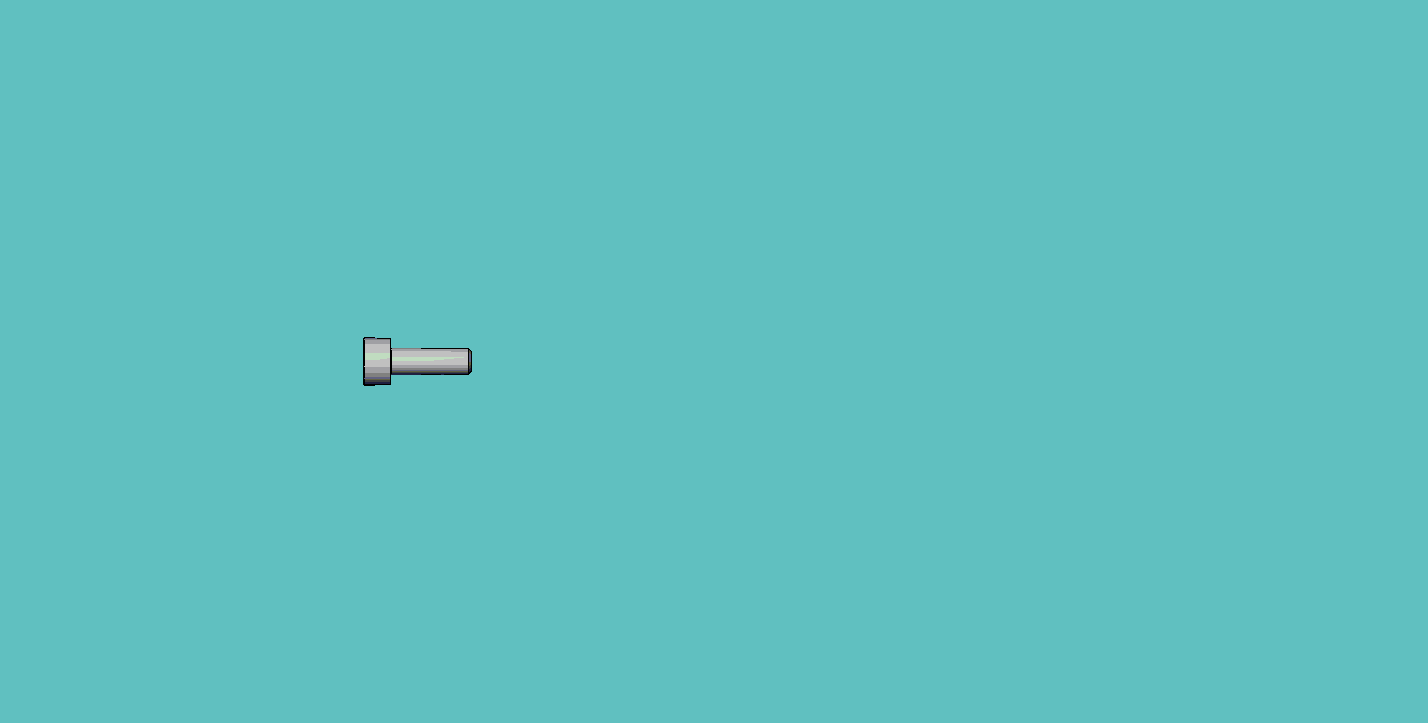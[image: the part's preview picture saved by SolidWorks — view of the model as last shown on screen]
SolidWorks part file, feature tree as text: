
SOLIDWORKS PART (.sldprt)
format: sldprt  version: not decoded by parser v0  size: 192,512 bytes
history: native  units: mm
features: sketch x4, plane x3, fillet x2, cut_revolve x2, material x1, revolve x1, thread x1, cut_extrude x1, pattern_linear x1 (+10 scaffold rows collapsed; 1 parser-record rows omitted)
feature tree (27):
  scaffold x10  (default folders/planes/origin — collapsed)
  material  "Material <not specified>"
  plane  "Plane1"
  plane  "Plane2"
  plane  "Plane3"
  parser-record x1  (decoder bookkeeping rows leaked as tree rows — omitted from the tree; the rows remain in map.json)
  revolve  "Base-Revolve"  [1 undecoded]
  sketch  "BodySke"  dims[c1.Head_fillet_rad=1.016mm c1.Head_top_radius=2.54mm c1.D1=19.05mm c1.Diameter=25.4mm c1.D3=50.8mm c1.D4=22.225mm c2.D4=45.0deg c2.D5=22.225mm c2.Head_ht=4.0mm c2.Length=12.0mm c2.D8=9.525mm c3.D8=45.0deg c3.D1=9.525mm c4.D8=9.525mm c5.D8=45.0deg c5.D1=73.025mm c6.D1=45.0deg c7.D1=9.525mm c8.D1=45.0deg c8.D4=22.225mm c9.D4=45.0deg c9.Thread_min=12.7mm c10.D4=9.525mm c10.Body_ch_ang=45.0deg c10.D8=22.225mm c11.D8=45.0deg c11.D5=22.225mm c12.D5=45.0deg c13.D5=~4.490128mm c14.D5=45.0deg c14.Head_dia=50.8mm c15.D5=~8.980256mm c15.Head_ch_ang=45.0deg c15.Head_side_ht=22.86mm c15.D9=19.05mm c15.Diameter=4.0mm c15.Head_dia=38.1mm c15.Minor_dia=3.22mm c15.Advance=0.7mm c15.Thread_nom=12.0mm c15.Thread_lim=~74.083342mm c15.Thread_length=60.0mm c16.Head_dia=7.0mm]
  thread  "ThreadCosmetic"  Diameter=9.9mm Thread_length=9.9mm Thread_minor=3.22mm  [1 undecoded]
  fillet  "Fillet1"  Radius=0.2mm Head_dia=7mm
  fillet  "Fillet2"  Radius=0.2mm
  sketch  "Sketch2"  dims[c1.D1=1.5355mm c1.D2=25.4mm c2.D2=60.0deg c2.Wall_thickness=11.427mm c2.Depth=2.0mm]
  cut_revolve  "Hex-PreBroach"  Angle=360deg
  sketch  "Sketch3"  dims[c1.D1=1.5355mm c1.D2=1.5355mm c1.Hex_size=3.071mm c1.D4=~14.664697mm c2.D4=120.0deg]
  cut_extrude  "Hex"  Depth=2mm Key_eng=2mm
  sketch  "ThdSchSke"  dims[c1.Thread_minor=~1.03886mm c1.Diameter=~1.413535mm c1.Start=~0.988134mm c1.D4=~4.446753mm c1.Vee=60.0deg c2.Thread_minor=~1.03886mm c2.Start=~2.540025mm c2.D1=~0.108159mm c2.D2=~0.108159mm c3.D1=~0.216319mm c3.SideAngle=55.0deg c3.D2=~0.216319mm c3.VeeAngle=70.0deg c3.Thread_minor=3.22mm c3.Overcut=5.0mm c3.Diameter=4.0mm c3.D6=~8.326268mm c4.D1=~8.326268mm c5.D1=90.0deg c5.Start=54.0mm c6.Start=6.1mm]
  cut_revolve  "ThreadSchematic"  Angle=360deg
  pattern_linear  "ThdSchPat"  Count1=15 Count2=1 Spacing1=0.66mm Spacing2=50mm Num_threads=15 Advance=0.66mm CopiedFlag=1
decode coverage: 11 of 12 modeling features carry decoded parameters
note: ~ marks probable driven/reference dimensions
note: 2 parameter values undecoded
note: suppression state not decoded; provenance and decode notes live in map.json
